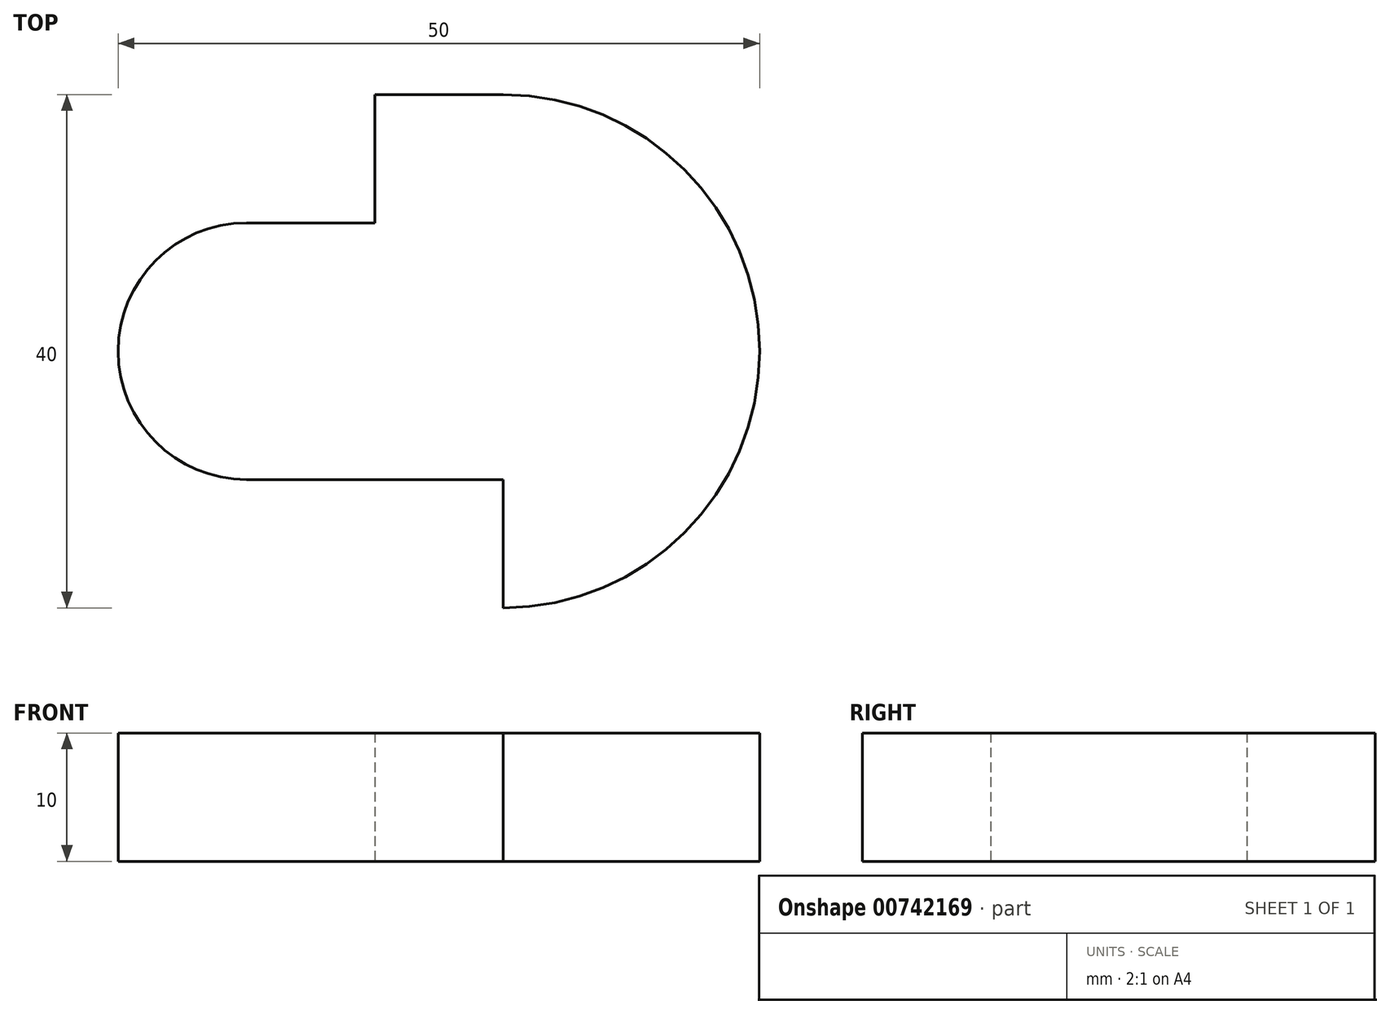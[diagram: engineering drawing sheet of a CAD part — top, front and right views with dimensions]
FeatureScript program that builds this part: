
annotation { "Feature Type Name" : "Feature", "Feature Type Description" : "" }
export const myFeature = defineFeature(function(context is Context, id is Id, definition is map)
    precondition{}
    {
        {
            var Q0;
            Q0=qCreatedBy(makeId("Top.planeOp"),FACE);
            var sketch = newSketch(context, id + "F0", { "sketchPlane" : qUnion([Q0])});
            skLineSegment(sketch, "E0", {"start": v(-28.65, 28.62) * mm, "end": v(-18.65, 28.62) * mm});
            skLineSegment(sketch, "E1", {"start": v(-18.65, 28.62) * mm, "end": v(-18.65, 38.62) * mm});
            skLineSegment(sketch, "E2", {"start": v(-18.65, 38.62) * mm, "end": v(-8.65, 38.62) * mm});
            skArc(sketch, "E3", {"start": v(-28.65, 28.62) * mm, "mid": v(-38.65, 18.62) * mm, "end": v(-28.65, 8.62) * mm});
            skLineSegment(sketch, "E4", {"start": v(-28.65, 8.62) * mm, "end": v(-8.65, 8.62) * mm});
            skLineSegment(sketch, "E5", {"start": v(-8.65, 8.62) * mm, "end": v(-8.65, -1.38) * mm});
            skArc(sketch, "E6", {"start": v(-8.65, -1.38) * mm, "mid": v(11.35, 18.62) * mm, "end": v(-8.65, 38.62) * mm});
            skSolve(sketch);
        }
        {
            var Q0;
            Q0=makeQuery(id+"F0.imprint","IMPRINT",FACE,{"disambiguationData":[TD([[makeQuery(id+"F0.imprint","IMPRINT",EDGE,{"derivedFrom":sQuery(id+"F0.wireOp",EDGE,"E0")}),-1.0]])]});
            extrude(context, id + "F1", {"entities" : qUnion([Q0]), "depth" : 10 * mm, "offsetDistance" : 25 * mm});
        }
    });
